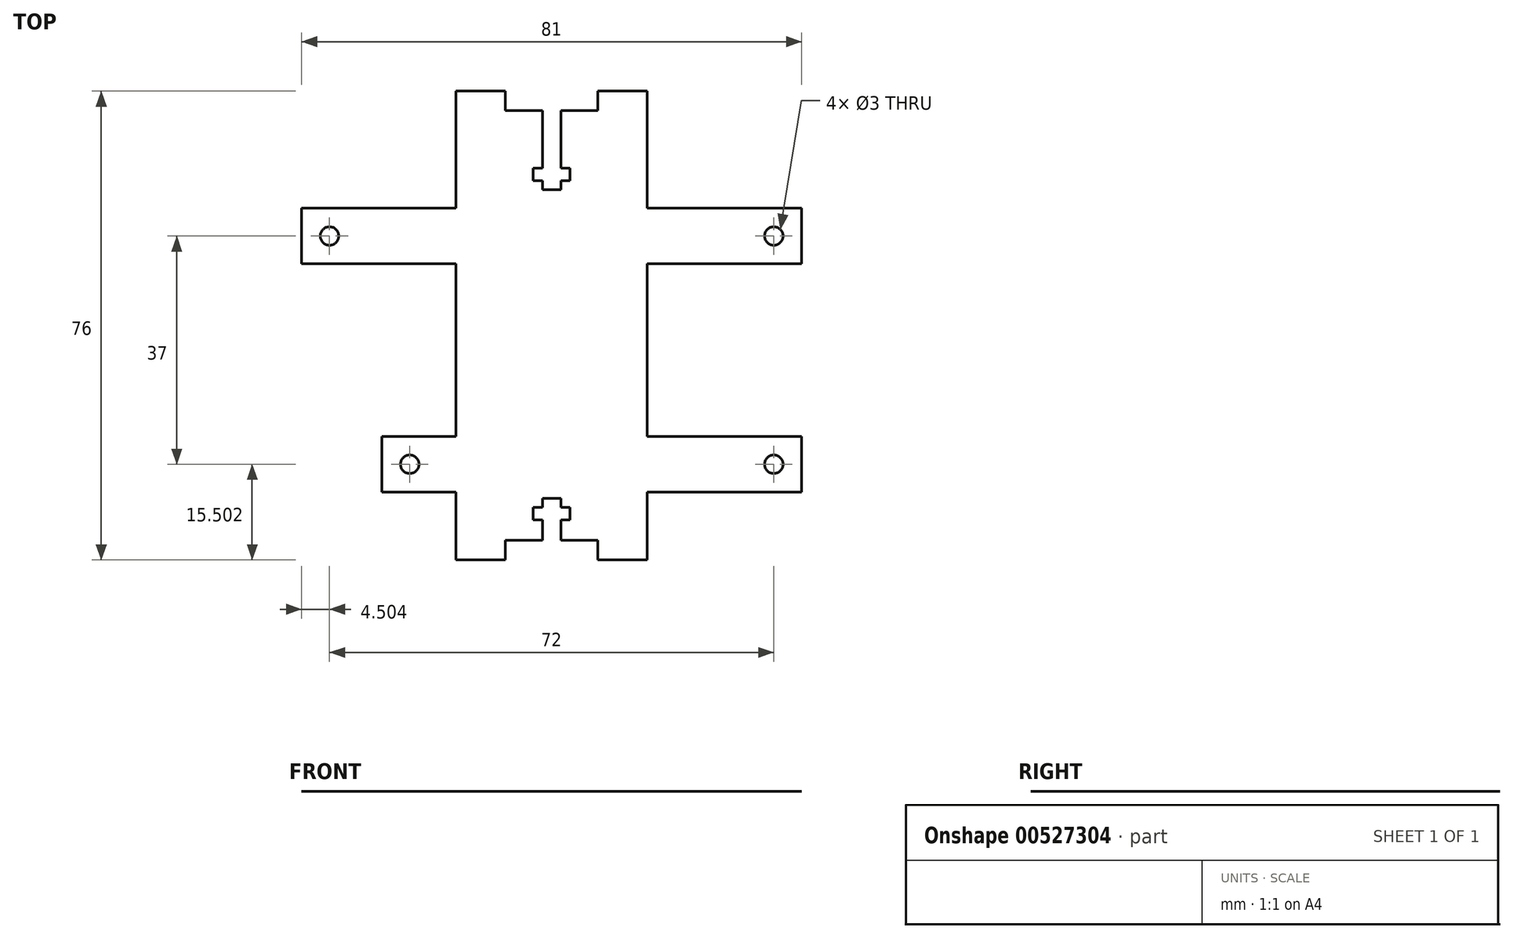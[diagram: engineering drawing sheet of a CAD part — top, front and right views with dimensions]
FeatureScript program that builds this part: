
annotation { "Feature Type Name" : "Feature", "Feature Type Description" : "" }
export const myFeature = defineFeature(function(context is Context, id is Id, definition is map)
    precondition{}
    {
        {
            var Q0;
            Q0=qCreatedBy(makeId("Top.planeOp"),FACE);
            var sketch = newSketch(context, id + "F0", { "sketchPlane" : qUnion([Q0])});
            skLineSegment(sketch, "E0.bottom", {"start": v(-18, 24.81) * mm, "end": v(63, 24.81) * mm});
            skLineSegment(sketch, "E0.top", {"start": v(-18, 15.81) * mm, "end": v(63, 15.81) * mm});
            skLineSegment(sketch, "E0.left", {"start": v(-18, 24.81) * mm, "end": v(-18, 15.81) * mm});
            skLineSegment(sketch, "E0.right", {"start": v(63, 24.81) * mm, "end": v(63, 15.81) * mm});
            skPoint(sketch, "E0.middle", {"position": v(22.5, 20.31) * mm});
            skCircle(sketch, "E1", {"center": v(-13.5, 20.31) * mm, "radius": 1.5 * mm});
            skLineSegment(sketch, "E2", {"start": v(22.5, 20.31) * mm, "end": v(22.5, 15.81) * mm});
            skCircle(sketch, "E3.MirrorC", {"center": v(58.5, 20.31) * mm, "radius": 1.5 * mm});
            skLineSegment(sketch, "E4.bottom", {"start": v(21, 43.81) * mm, "end": v(24, 43.81) * mm});
            skLineSegment(sketch, "E4.top", {"start": v(21, 27.81) * mm, "end": v(24, 27.81) * mm});
            skLineSegment(sketch, "E4.left", {"start": v(21, 43.81) * mm, "end": v(21, 27.81) * mm});
            skLineSegment(sketch, "E4.right", {"start": v(24, 43.81) * mm, "end": v(24, 27.81) * mm});
            skPoint(sketch, "E4.middle", {"position": v(22.5, 35.81) * mm});
            skLineSegment(sketch, "E5.bottom", {"start": v(19.5, 31.31) * mm, "end": v(25.5, 31.31) * mm});
            skLineSegment(sketch, "E5.top", {"start": v(19.5, 29.31) * mm, "end": v(25.5, 29.31) * mm});
            skLineSegment(sketch, "E5.left", {"start": v(19.5, 31.31) * mm, "end": v(19.5, 29.31) * mm});
            skLineSegment(sketch, "E5.right", {"start": v(25.5, 31.31) * mm, "end": v(25.5, 29.31) * mm});
            skPoint(sketch, "E5.middle", {"position": v(22.5, 30.31) * mm});
            skLineSegment(sketch, "E6.bottom", {"start": v(30, 43.81) * mm, "end": v(38, 43.81) * mm});
            skLineSegment(sketch, "E6.top", {"start": v(30, 40.64) * mm, "end": v(38, 40.64) * mm});
            skLineSegment(sketch, "E6.left", {"start": v(30, 43.81) * mm, "end": v(30, 40.64) * mm});
            skLineSegment(sketch, "E6.right", {"start": v(38, 43.81) * mm, "end": v(38, 40.64) * mm});
            skLineSegment(sketch, "E7", {"start": v(22.5, 35.81) * mm, "end": v(22.5, 30.31) * mm});
            skLineSegment(sketch, "E8.MirrorCS", {"start": v(15, 43.81) * mm, "end": v(15, 40.64) * mm});
            skLineSegment(sketch, "E9.MirrorCS", {"start": v(15, 43.81) * mm, "end": v(7, 43.81) * mm});
            skLineSegment(sketch, "E10.MirrorCS", {"start": v(15, 40.64) * mm, "end": v(7, 40.64) * mm});
            skLineSegment(sketch, "E11.MirrorCS", {"start": v(7, 43.81) * mm, "end": v(7, 40.64) * mm});
            skLineSegment(sketch, "E12", {"start": v(15, 40.64) * mm, "end": v(30, 40.64) * mm});
            skLineSegment(sketch, "E13", {"start": v(7, 40.64) * mm, "end": v(7, 24.81) * mm});
            skLineSegment(sketch, "E14", {"start": v(38, 40.64) * mm, "end": v(38, 24.81) * mm});
            skLineSegment(sketch, "E15.bottom", {"start": v(21, -22.19) * mm, "end": v(24, -22.19) * mm});
            skLineSegment(sketch, "E15.top", {"start": v(21, -32.19) * mm, "end": v(24, -32.19) * mm});
            skLineSegment(sketch, "E15.left", {"start": v(21, -22.19) * mm, "end": v(21, -32.19) * mm});
            skLineSegment(sketch, "E15.right", {"start": v(24, -22.19) * mm, "end": v(24, -32.19) * mm});
            skPoint(sketch, "E15.middle", {"position": v(22.5, -27.19) * mm});
            skLineSegment(sketch, "E16.bottom", {"start": v(19.5, -25.69) * mm, "end": v(25.5, -25.69) * mm});
            skLineSegment(sketch, "E16.top", {"start": v(19.5, -23.69) * mm, "end": v(25.5, -23.69) * mm});
            skLineSegment(sketch, "E16.left", {"start": v(19.5, -25.69) * mm, "end": v(19.5, -23.69) * mm});
            skLineSegment(sketch, "E16.right", {"start": v(25.5, -25.69) * mm, "end": v(25.5, -23.69) * mm});
            skPoint(sketch, "E16.middle", {"position": v(22.5, -24.69) * mm});
            skLineSegment(sketch, "E17.bottom", {"start": v(15, -32.19) * mm, "end": v(7, -32.19) * mm});
            skLineSegment(sketch, "E17.top", {"start": v(15, -29.01) * mm, "end": v(7, -29.01) * mm});
            skLineSegment(sketch, "E17.left", {"start": v(15, -32.19) * mm, "end": v(15, -29.01) * mm});
            skLineSegment(sketch, "E17.right", {"start": v(7, -32.19) * mm, "end": v(7, -29.01) * mm});
            skLineSegment(sketch, "E18", {"start": v(22.5, -24.69) * mm, "end": v(22.5, -27.19) * mm});
            skLineSegment(sketch, "E19.MirrorCS", {"start": v(30, -32.19) * mm, "end": v(30, -29.01) * mm});
            skLineSegment(sketch, "E20.MirrorCS", {"start": v(30, -29.01) * mm, "end": v(38, -29.01) * mm});
            skLineSegment(sketch, "E21.MirrorCS", {"start": v(38, -32.19) * mm, "end": v(38, -29.01) * mm});
            skLineSegment(sketch, "E22.MirrorCS", {"start": v(30, -32.19) * mm, "end": v(38, -32.19) * mm});
            skLineSegment(sketch, "E23", {"start": v(7, -29.01) * mm, "end": v(7, 15.81) * mm});
            skLineSegment(sketch, "E24", {"start": v(38, -29.01) * mm, "end": v(38, 15.81) * mm});
            skLineSegment(sketch, "E25", {"start": v(15, -29.01) * mm, "end": v(30, -29.01) * mm});
            skCircle(sketch, "E26", {"center": v(58.5, -16.69) * mm, "radius": 1.5 * mm});
            skCircle(sketch, "E27", {"center": v(-0.5, -16.69) * mm, "radius": 1.5 * mm});
            skLineSegment(sketch, "E28.bottom", {"start": v(-5, -21.19) * mm, "end": v(63, -21.19) * mm});
            skLineSegment(sketch, "E28.top", {"start": v(-5, -12.19) * mm, "end": v(63, -12.19) * mm});
            skLineSegment(sketch, "E28.left", {"start": v(-5, -21.19) * mm, "end": v(-5, -12.19) * mm});
            skLineSegment(sketch, "E28.right", {"start": v(63, -21.19) * mm, "end": v(63, -12.19) * mm});
            skSolve(sketch);
        }
        {
            var Q0;
            Q0=makeQuery(id+"F0.imprint","IMPRINT",FACE,{"disambiguationData":[TD([[makeQuery(id+"F0.imprint","IMPRINT",EDGE,{"derivedFrom":sQuery(id+"F0.wireOp",EDGE,"E0.bottom")}),-1.0]])]});
            var Q1;
            {var subQ7=sQuery(id+"F0.wireOp",EDGE,"E4.top");Q1=makeQuery(id+"F0.imprint","IMPRINT",FACE,{"disambiguationData":[TD([[makeQuery(id+"F0.imprint","IMPRINT",EDGE,{"derivedFrom":subQ7}),-1.0]])]});}
            var Q2;
            Q2=makeQuery(id+"F0.imprint","IMPRINT",FACE,{"disambiguationData":[TD([[makeQuery(id+"F0.imprint","IMPRINT",EDGE,{"derivedFrom":sQuery(id+"F0.wireOp",EDGE,"E8.MirrorCS")}),-1.0]])]});
            var Q3;
            Q3=makeQuery(id+"F0.imprint","IMPRINT",FACE,{"disambiguationData":[TD([[makeQuery(id+"F0.imprint","IMPRINT",EDGE,{"derivedFrom":sQuery(id+"F0.wireOp",EDGE,"E6.bottom")}),-1.0]])]});
            var Q4;
            {var subQ16=sQuery(id+"F0.wireOp",EDGE,"E15.bottom");Q4=makeQuery(id+"F0.imprint","IMPRINT",FACE,{"disambiguationData":[TD([[makeQuery(id+"F0.imprint","IMPRINT",EDGE,{"derivedFrom":subQ16}),1.0]])]});}
            var Q5;
            Q5=makeQuery(id+"F0.imprint","IMPRINT",FACE,{"disambiguationData":[TD([[makeQuery(id+"F0.imprint","IMPRINT",EDGE,{"derivedFrom":sQuery(id+"F0.wireOp",EDGE,"E17.bottom")}),-1.0]])]});
            var Q6;
            Q6=makeQuery(id+"F0.imprint","IMPRINT",FACE,{"disambiguationData":[TD([[makeQuery(id+"F0.imprint","IMPRINT",EDGE,{"derivedFrom":sQuery(id+"F0.wireOp",EDGE,"E19.MirrorCS")}),-1.0]])]});
            var Q7;
            {var subQ1=sQuery(id+"F0.wireOp",EDGE,"E0.top");var subQ8=makeQuery(id+"F0.imprint","IMPRINT",VERTEX,{"derivedFrom":subQ1});Q7=makeQuery(id+"F0.imprint","IMPRINT",FACE,{"disambiguationData":[TD([[makeQuery(id+"F0.imprint","IMPRINT",EDGE,{"disambiguationData":[TD([[subQ8,1.0]])],"derivedFrom":subQ1}),-1.0]])]});}
            var Q8;
            {var subQ0=sQuery(id+"F0.wireOp",EDGE,"1zIilXki-0rrE-mewM-yc4W-awrqwXFVErq0.bottom");var subQ1=sQuery(id+"F0.wireOp",EDGE,"E23");var subQ2=makeQuery(id+"F0.imprint","INTERSECT",VERTEX,{"derivedFrom":[subQ1,subQ0]});Q8=makeQuery(id+"F0.imprint","IMPRINT",FACE,{"disambiguationData":[TD([[makeQuery(id+"F0.imprint","IMPRINT",EDGE,{"disambiguationData":[TD([[subQ2,-1.0]])],"derivedFrom":subQ1}),-1.0]])]});}
            var Q9;
            Q9=makeQuery(id+"F0.imprint","IMPRINT",FACE,{"disambiguationData":[TD([[makeQuery(id+"F0.imprint","IMPRINT",EDGE,{"derivedFrom":sQuery(id+"F0.wireOp",EDGE,"ef4f6fd7-b101-49b2-9d93-8d79d9c1be9c0.MirrorC")}),1.0]])]});
            var Q10;
            Q10=makeQuery(id+"F0.imprint","IMPRINT",FACE,{"disambiguationData":[TD([[makeQuery(id+"F0.imprint","IMPRINT",EDGE,{"derivedFrom":sQuery(id+"F0.wireOp",EDGE,"LNEiIDFf-A2mT-8AOw-AQnD-ryaXKdFsubHj")}),-1.0]])]});
            var Q11;
            {var subQ4=sQuery(id+"F0.wireOp",EDGE,"E27");Q11=makeQuery(id+"F0.imprint","IMPRINT",FACE,{"disambiguationData":[TD([[makeQuery(id+"F0.imprint","IMPRINT",EDGE,{"derivedFrom":subQ4}),-1.0]])]});}
            var Q12;
            Q12=makeQuery(id+"F0.imprint","IMPRINT",FACE,{"disambiguationData":[TD([[makeQuery(id+"F0.imprint","IMPRINT",EDGE,{"derivedFrom":sQuery(id+"F0.wireOp",EDGE,"E26")}),-1.0]])]});
            extrude(context, id + "F1", {"entities" : qUnion([Q0, Q1, Q2, Q3, Q4, Q5, Q6, Q7, Q8, Q9, Q10, Q11, Q12]), "depth" : 1 / 203.2 * mm, "offsetDistance" : 25 * mm});
        }
    });
